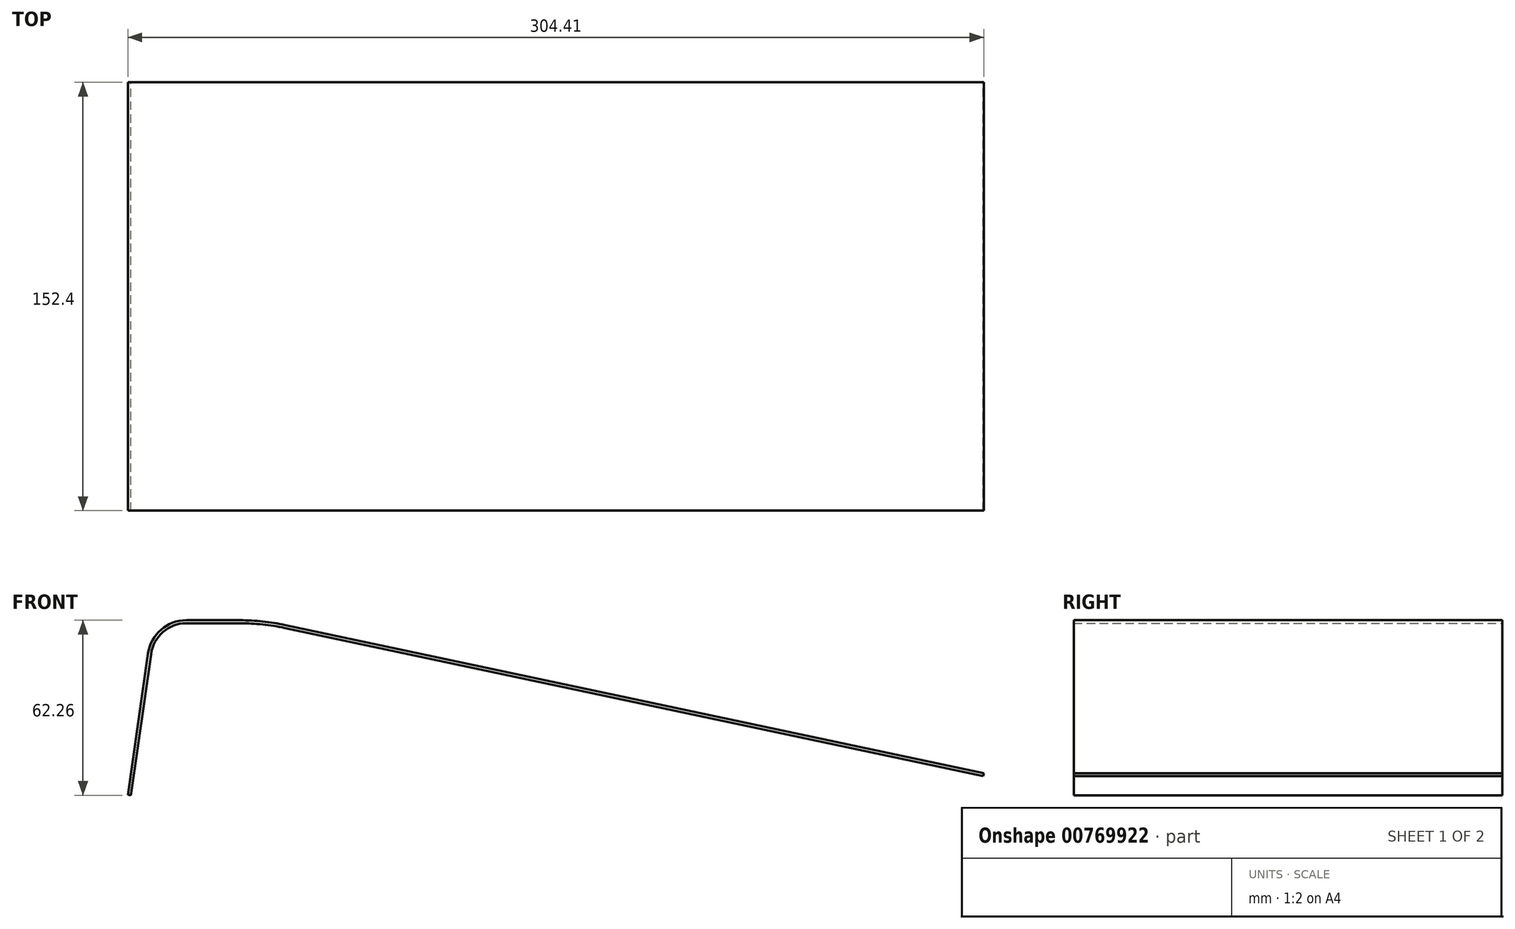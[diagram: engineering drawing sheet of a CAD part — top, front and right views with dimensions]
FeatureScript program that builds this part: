
annotation { "Feature Type Name" : "Feature", "Feature Type Description" : "" }
export const myFeature = defineFeature(function(context is Context, id is Id, definition is map)
    precondition{}
    {
        {
            var Q0;
            Q0=qCreatedBy(makeId("Front.planeOp"),FACE);
            var sketch = newSketch(context, id + "F0", { "sketchPlane" : qUnion([Q0])});
            skLineSegment(sketch, "E0", {"start": v(49.11, 266.7) * mm, "end": v(68.2, 266.7) * mm});
            skLineSegment(sketch, "E1", {"start": v(84.02, 265.04) * mm, "end": v(332.5, 212.34) * mm});
            skLineSegment(sketch, "E2", {"start": v(-73.41, 146.05) * mm, "end": v(634.9, 146.05) * mm, "construction": true});
            skPoint(sketch, "E3.visualSharp", {"position": v(38.1, 266.7) * mm});
            skArc(sketch, "E3.filletArc", {"start": v(49.11, 266.7) * mm, "mid": v(40.8, 263.6) * mm, "end": v(36.54, 255.8) * mm});
            skPoint(sketch, "E4.visualSharp", {"position": v(76.2, 266.7) * mm});
            skArc(sketch, "E4.filletArc", {"start": v(84.02, 265.04) * mm, "mid": v(76.16, 266.28) * mm, "end": v(68.2, 266.7) * mm});
            skArc(sketch, "E5.1", {"start": v(84.24, 266.09) * mm, "mid": v(76.27, 267.35) * mm, "end": v(68.2, 267.77) * mm});
            skLineSegment(sketch, "E5.2", {"start": v(49.11, 267.77) * mm, "end": v(68.2, 267.77) * mm});
            skArc(sketch, "E5.3", {"start": v(49.11, 267.77) * mm, "mid": v(40.1, 264.4) * mm, "end": v(35.49, 255.95) * mm});
            skLineSegment(sketch, "E5.5", {"start": v(84.24, 266.09) * mm, "end": v(332.71, 213.38) * mm});
            skLineSegment(sketch, "E6", {"start": v(0, 0) * mm, "end": v(-1.06, 0.15) * mm});
            skPoint(sketch, "E7", {"position": v(29.36, 205.5) * mm});
            skPoint(sketch, "E8", {"position": v(332.5, 212.34) * mm});
            skLineSegment(sketch, "E9", {"start": v(29.36, 205.5) * mm, "end": v(28.3, 205.66) * mm});
            skLineSegment(sketch, "E10", {"start": v(332.5, 212.34) * mm, "end": v(332.71, 213.38) * mm});
            skLineSegment(sketch, "E11.trimOffspring", {"start": v(29.36, 205.5) * mm, "end": v(36.54, 255.8) * mm});
            skLineSegment(sketch, "E12.trimOffspring", {"start": v(28.3, 205.66) * mm, "end": v(35.49, 255.95) * mm});
            skSolve(sketch);
        }
        {
            var Q0;
            Q0 = qSketchRegion(id + "F0", true);
            extrude(context, id + "F1", {"entities" : qUnion([Q0]), "depth" : 152.4 * mm, "offsetDistance" : 25.4 * mm});
        }
    });
